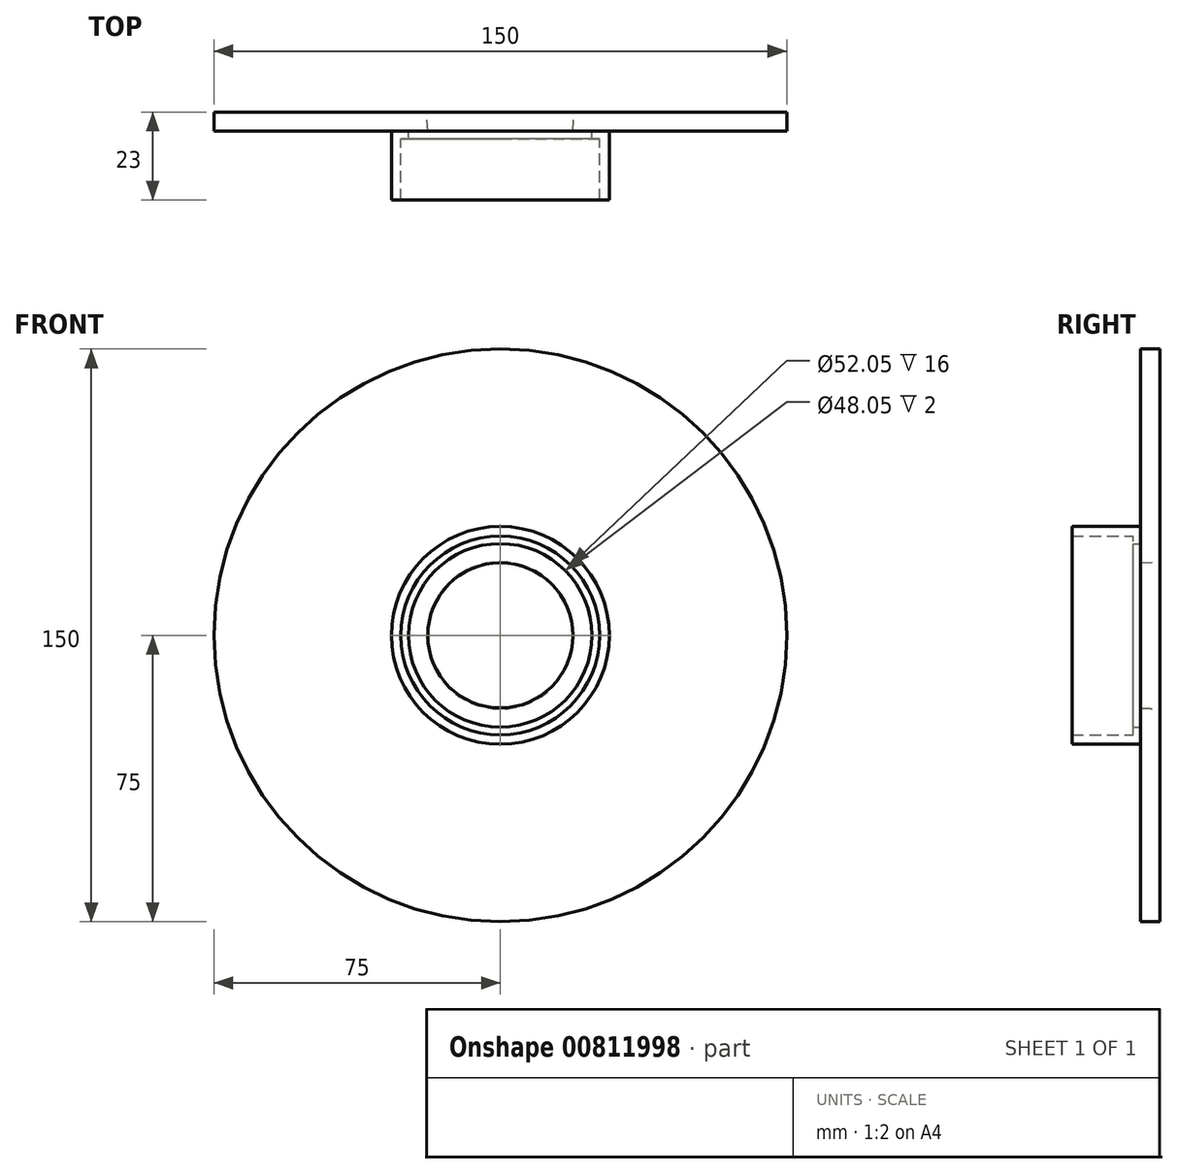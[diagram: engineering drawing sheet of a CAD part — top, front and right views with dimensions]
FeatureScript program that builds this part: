
annotation { "Feature Type Name" : "Feature", "Feature Type Description" : "" }
export const myFeature = defineFeature(function(context is Context, id is Id, definition is map)
    precondition{}
    {
        {
            var Q0;
            Q0=qCreatedBy(makeId("Front.planeOp"),FACE);
            var sketch = newSketch(context, id + "F0", { "sketchPlane" : qUnion([Q0])});
            skCircle(sketch, "E0", {"center": v(0, 0) * mm, "radius": 75 * mm});
            skSolve(sketch);
        }
        {
            var Q0;
            Q0 = qSketchRegion(id + "F0", true);
            extrude(context, id + "F1", {"entities" : qUnion([Q0]), "depth" : 5 * mm, "offsetDistance" : 25 * mm});
        }
        {
            var Q0;
            Q0=makeQuery(id+"F1.opExtrude","CAP_FACE",FACE,{"disambiguationData":[OSD([sQuery(id+"F0.wireOp",EDGE,"E0")])],"isStart":false});
            var sketch = newSketch(context, id + "F2", { "sketchPlane" : qUnion([Q0])});
            skCircle(sketch, "E1", {"center": v(0, 0) * mm, "radius": 19 * mm});
            skSolve(sketch);
        }
        {
            var Q0;
            Q0=makeQuery(id+"F2.imprint","IMPRINT",FACE,{"disambiguationData":[TD([[makeQuery(id+"F2.imprint","IMPRINT",EDGE,{"derivedFrom":sQuery(id+"F2.wireOp",EDGE,"E1")}),1.0]])]});
            extrude(context, id + "F3", {"entities" : qUnion([Q0]), "operationType" : NewBodyOperationType.REMOVE, "endBound" : BoundingType.UP_TO_NEXT, "oppositeDirection" : true, "depth" : 25 * mm, "offsetDistance" : 25 * mm, "hasDraft" : true, "draftAngle" : 3 * degree});
        }
        {
            var Q0;
            Q0=makeQuery(id+"F1.opExtrude","CAP_FACE",FACE,{"disambiguationData":[OSD([sQuery(id+"F0.wireOp",EDGE,"E0")])],"isStart":false});
            var sketch = newSketch(context, id + "F4", { "sketchPlane" : qUnion([Q0])});
            skCircle(sketch, "E2", {"center": v(0, 0) * mm, "radius": 26.02 * mm});
            skCircle(sketch, "E3", {"center": v(0, 0) * mm, "radius": 28.52 * mm});
            skSolve(sketch);
        }
        {
            var Q0;
            Q0=makeQuery(id+"F4.imprint","IMPRINT",FACE,{"disambiguationData":[TD([[makeQuery(id+"F4.imprint","IMPRINT",EDGE,{"derivedFrom":sQuery(id+"F4.wireOp",EDGE,"E2")}),-1.0]])]});
            extrude(context, id + "F5", {"entities" : qUnion([Q0]), "operationType" : NewBodyOperationType.ADD, "depth" : 18 * mm, "offsetDistance" : 25 * mm});
        }
        {
            var Q0;
            Q0=makeQuery(id+"F5.boolean.opBoolean","SPLIT",FACE,{"disambiguationData":[TD([makeQuery(id+"F3.boolean.opBoolean","COPY",FACE,{"derivedFrom":makeQuery(id+"F3.opExtrude","SWEPT_FACE",FACE,{"disambiguationData":[OSD([sQuery(id+"F2.wireOp",EDGE,"E1")])]})})])],"derivedFrom":makeQuery(id+"F1.opExtrude","CAP_FACE",FACE,{"disambiguationData":[OSD([sQuery(id+"F0.wireOp",EDGE,"E0")])],"isStart":false})});
            var sketch = newSketch(context, id + "F6", { "sketchPlane" : qUnion([Q0])});
            skCircle(sketch, "E4", {"center": v(0, 0) * mm, "radius": 26.02 * mm});
            skCircle(sketch, "E5", {"center": v(0, 0) * mm, "radius": 24.02 * mm});
            skSolve(sketch);
        }
        {
            var Q0;
            Q0=makeQuery(id+"F6.imprint","IMPRINT",FACE,{"disambiguationData":[TD([[makeQuery(id+"F6.imprint","IMPRINT",EDGE,{"derivedFrom":sQuery(id+"F6.wireOp",EDGE,"E4")}),1.0]])]});
            var Q1;
            Q1=sQuery(id+"F6.wireOp",EDGE,"E4");
            var Q2;
            Q2=sQuery(id+"F6.wireOp",EDGE,"E5");
            extrude(context, id + "F7", {"entities" : qUnion([Q0]), "operationType" : NewBodyOperationType.ADD, "surfaceEntities" : qUnion([Q1, Q2]), "depth" : 2 * mm, "offsetDistance" : 25 * mm});
        }
    });
